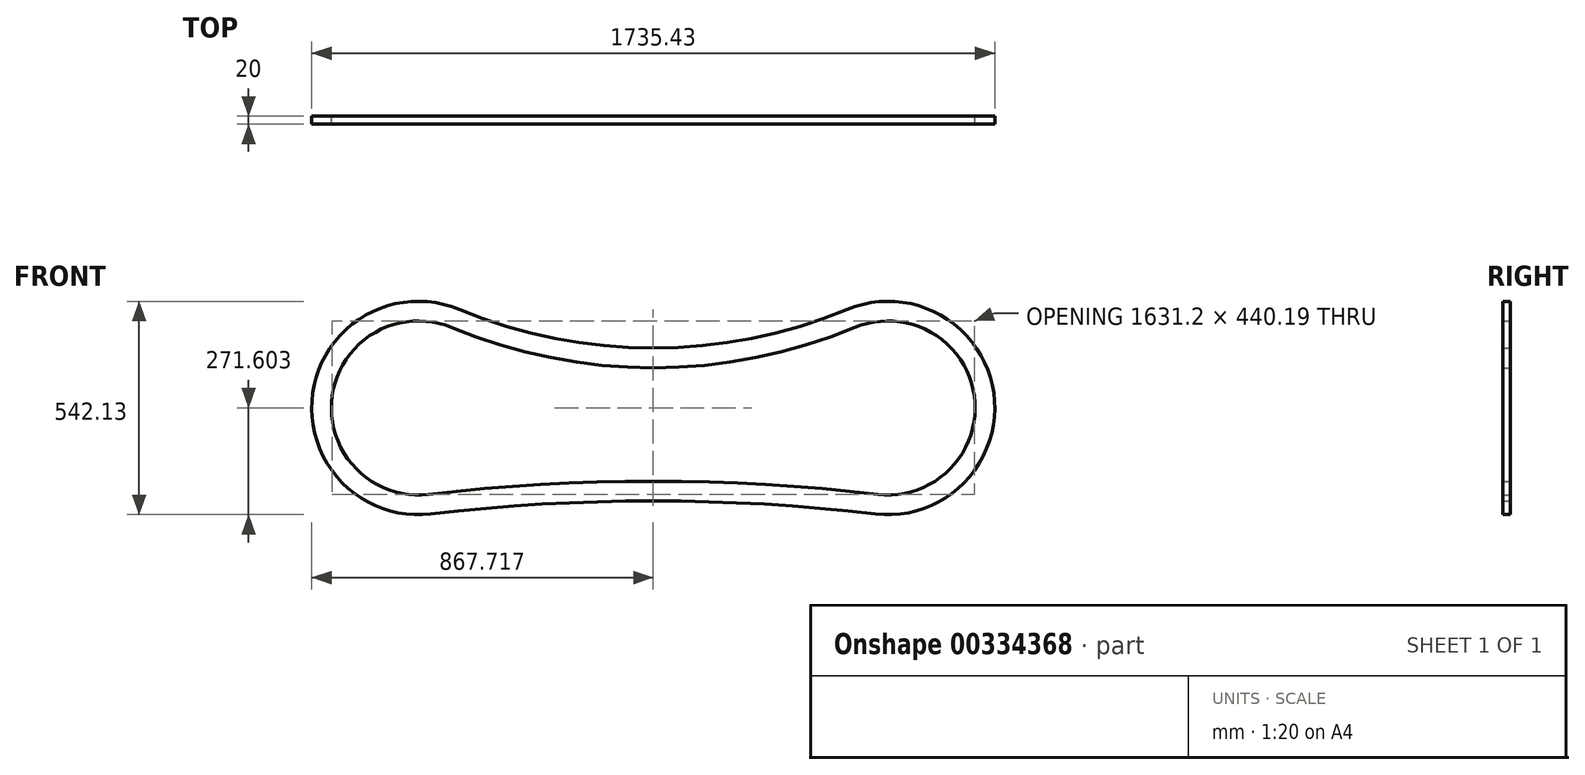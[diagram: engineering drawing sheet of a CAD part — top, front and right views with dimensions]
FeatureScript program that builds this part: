
annotation { "Feature Type Name" : "Feature", "Feature Type Description" : "" }
export const myFeature = defineFeature(function(context is Context, id is Id, definition is map)
    precondition{}
    {
        {
            var Q0;
            Q0=qCreatedBy(makeId("Front.planeOp"),FACE);
            var sketch = newSketch(context, id + "F0", { "sketchPlane" : qUnion([Q0])});
            skArc(sketch, "E0", {"start": v(-489.5, 261.23) * mm, "mid": v(-862, 48.35) * mm, "end": v(-561.95, -258.3) * mm});
            skArc(sketch, "E1", {"start": v(568.19, -258.3) * mm, "mid": v(868.24, 48.35) * mm, "end": v(495.74, 261.23) * mm});
            skArc(sketch, "E2", {"start": v(568.19, -258.3) * mm, "mid": v(3.12, -225.27) * mm, "end": v(-561.95, -258.3) * mm});
            skPoint(sketch, "E2.centerSnap0", {"position": v(3.12, 10.92) * mm});
            skArc(sketch, "E3", {"start": v(-489.5, 261.23) * mm, "mid": v(3.12, 162.94) * mm, "end": v(495.74, 261.23) * mm});
            skArc(sketch, "E4.0", {"start": v(-508.7, 215.06) * mm, "mid": v(-812.48, 41.45) * mm, "end": v(-567.78, -208.64) * mm});
            skArc(sketch, "E4.1", {"start": v(-508.7, 215.06) * mm, "mid": v(3.12, 112.94) * mm, "end": v(514.93, 215.06) * mm});
            skArc(sketch, "E4.2", {"start": v(574.01, -208.64) * mm, "mid": v(818.72, 41.45) * mm, "end": v(514.93, 215.06) * mm});
            skArc(sketch, "E4.3", {"start": v(574.01, -208.64) * mm, "mid": v(3.12, -175.27) * mm, "end": v(-567.78, -208.64) * mm});
            skSolve(sketch);
        }
        {
            var Q0;
            Q0=makeQuery(id+"F0.imprint","IMPRINT",FACE,{"disambiguationData":[TD([[makeQuery(id+"F0.imprint","IMPRINT",EDGE,{"derivedFrom":sQuery(id+"F0.wireOp",EDGE,"E0")}),1.0]])]});
            extrude(context, id + "F1", {"entities" : qUnion([Q0]), "depth" : 20 * mm});
        }
    });
